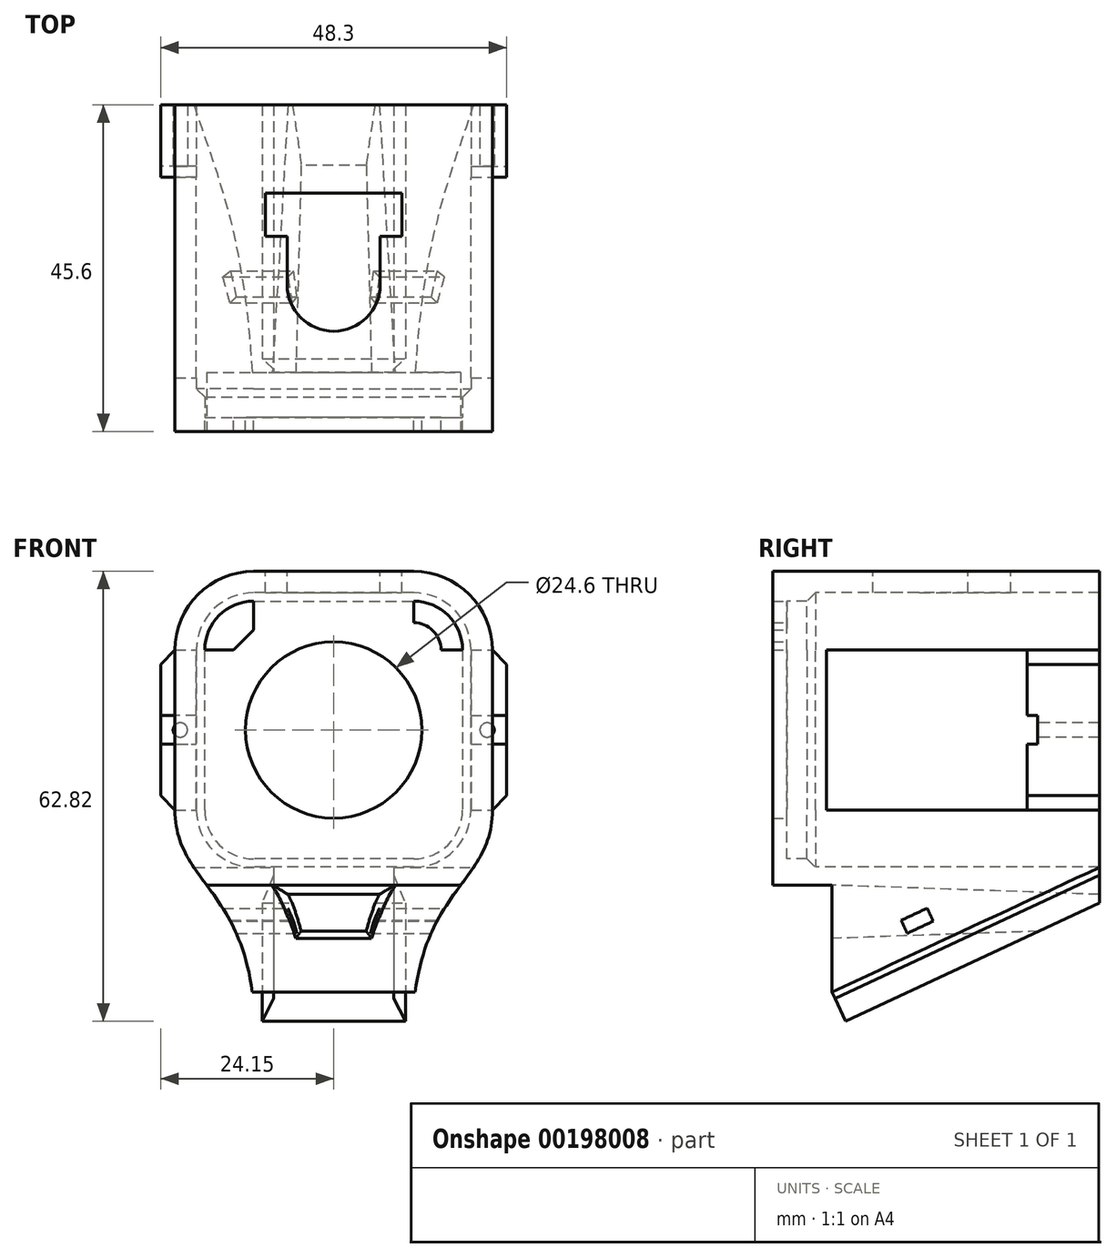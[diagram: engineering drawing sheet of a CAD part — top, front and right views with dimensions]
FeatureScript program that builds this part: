
annotation { "Feature Type Name" : "Feature", "Feature Type Description" : "" }
export const myFeature = defineFeature(function(context is Context, id is Id, definition is map)
    precondition{}
    {
        {
            var Q0;
            Q0=qCreatedBy(makeId("Front.planeOp"),FACE);
            var sketch = newSketch(context, id + "F0", { "sketchPlane" : qUnion([Q0])});
            skLineSegment(sketch, "E0.bottom", {"start": v(11.15, 19.15) * mm, "end": v(-11.15, 19.15) * mm});
            skLineSegment(sketch, "E0.top", {"start": v(11.15, -19.15) * mm, "end": v(-11.15, -19.15) * mm});
            skLineSegment(sketch, "E0.left", {"start": v(19.15, 11.15) * mm, "end": v(19.15, -11.15) * mm});
            skLineSegment(sketch, "E0.right", {"start": v(-19.15, 11.15) * mm, "end": v(-19.15, -11.15) * mm});
            skPoint(sketch, "E0.middle", {"position": v(0, 0) * mm});
            skPoint(sketch, "E1.visualSharp", {"position": v(-19.15, 19.15) * mm});
            skArc(sketch, "E1.filletArc", {"start": v(-11.15, 19.15) * mm, "mid": v(-16.8, 16.8) * mm, "end": v(-19.15, 11.15) * mm});
            skPoint(sketch, "E2.visualSharp", {"position": v(19.15, 19.15) * mm});
            skArc(sketch, "E2.filletArc", {"start": v(19.15, 11.15) * mm, "mid": v(16.8, 16.8) * mm, "end": v(11.15, 19.15) * mm});
            skPoint(sketch, "E3.visualSharp", {"position": v(19.15, -19.15) * mm});
            skArc(sketch, "E3.filletArc", {"start": v(11.15, -19.15) * mm, "mid": v(16.8, -16.8) * mm, "end": v(19.15, -11.15) * mm});
            skPoint(sketch, "E4.visualSharp", {"position": v(-19.15, -19.15) * mm});
            skArc(sketch, "E4.filletArc", {"start": v(-19.15, -11.15) * mm, "mid": v(-16.8, -16.8) * mm, "end": v(-11.15, -19.15) * mm});
            skLineSegment(sketch, "E5.0", {"start": v(11.15, 22.15) * mm, "end": v(-11.15, 22.15) * mm});
            skArc(sketch, "E5.1", {"start": v(22.15, 11.15) * mm, "mid": v(18.93, 18.93) * mm, "end": v(11.15, 22.15) * mm});
            skArc(sketch, "E5.2", {"start": v(-11.15, 22.15) * mm, "mid": v(-18.93, 18.93) * mm, "end": v(-22.15, 11.15) * mm});
            skLineSegment(sketch, "E5.3", {"start": v(22.15, 11.15) * mm, "end": v(22.15, -11.15) * mm});
            skLineSegment(sketch, "E5.4", {"start": v(-22.15, 11.15) * mm, "end": v(-22.15, -11.15) * mm});
            skArc(sketch, "E5.5", {"start": v(-22.15, -11.15) * mm, "mid": v(-18.93, -18.93) * mm, "end": v(-11.15, -22.15) * mm});
            skLineSegment(sketch, "E5.6", {"start": v(11.15, -22.15) * mm, "end": v(-11.15, -22.15) * mm});
            skArc(sketch, "E5.7", {"start": v(11.15, -22.15) * mm, "mid": v(18.93, -18.93) * mm, "end": v(22.15, -11.15) * mm});
            skLineSegment(sketch, "E6.0", {"start": v(11.15, 17.98) * mm, "end": v(-11.15, 17.98) * mm});
            skArc(sketch, "E6.1", {"start": v(17.98, 11.15) * mm, "mid": v(15.98, 15.98) * mm, "end": v(11.15, 17.98) * mm});
            skArc(sketch, "E6.2", {"start": v(-11.15, 17.98) * mm, "mid": v(-15.98, 15.98) * mm, "end": v(-17.98, 11.15) * mm});
            skLineSegment(sketch, "E6.3", {"start": v(17.98, 11.15) * mm, "end": v(17.98, -11.15) * mm});
            skLineSegment(sketch, "E6.4", {"start": v(-17.98, 11.15) * mm, "end": v(-17.98, -11.15) * mm});
            skArc(sketch, "E6.5", {"start": v(-17.98, -11.15) * mm, "mid": v(-15.98, -15.98) * mm, "end": v(-11.15, -17.98) * mm});
            skLineSegment(sketch, "E6.6", {"start": v(11.15, -17.98) * mm, "end": v(-11.15, -17.98) * mm});
            skArc(sketch, "E6.7", {"start": v(11.15, -17.98) * mm, "mid": v(15.98, -15.98) * mm, "end": v(17.98, -11.15) * mm});
            skFitSpline(sketch, "E7", {"points": [v(-22.15, -11.15) * mm, v(-11, -42.15) * mm], "startDerivative": vector(0, -32.02) * mm, "endDerivative": vector(0.45, -60) * mm});
            skLineSegment(sketch, "E8", {"start": v(-22.15, -11.15) * mm, "end": v(-22.15, -23.53) * mm, "construction": true});
            skPoint(sketch, "E9", {"position": v(-22.15, -17.34) * mm});
            skLineSegment(sketch, "E10", {"start": v(-11, -42.15) * mm, "end": v(0, -42.15) * mm});
            skLineSegment(sketch, "E11", {"start": v(0, -42.15) * mm, "end": v(0, -22.15) * mm, "construction": true});
            skLineSegment(sketch, "E12.MirrorCS", {"start": v(11, -42.15) * mm, "end": v(0, -42.15) * mm});
            skFitSpline(sketch, "E13.MirrorCS", {"points": [v(22.15, -11.15) * mm, v(11, -42.15) * mm], "startDerivative": vector(0, -32.02) * mm, "endDerivative": vector(-0.45, -60) * mm});
            skSolve(sketch);
        }
        {
            var Q0;
            Q0=makeQuery(id+"F0.imprint","IMPRINT",FACE,{"disambiguationData":[TD([[makeQuery(id+"F0.imprint","IMPRINT",EDGE,{"derivedFrom":sQuery(id+"F0.wireOp",EDGE,"E0.bottom")}),-1.0]])]});
            var Q1;
            Q1=makeQuery(id+"F0.imprint","IMPRINT",FACE,{"disambiguationData":[TD([[makeQuery(id+"F0.imprint","IMPRINT",EDGE,{"derivedFrom":sQuery(id+"F0.wireOp",EDGE,"E5.5")}),-1.0]])]});
            extrude(context, id + "F1", {"entities" : qUnion([Q0, Q1]), "oppositeDirection" : true, "depth" : 43.6 * mm});
        }
        {
            var Q0;
            Q0=makeQuery(id+"F0.imprint","IMPRINT",FACE,{"disambiguationData":[TD([[makeQuery(id+"F0.imprint","IMPRINT",EDGE,{"derivedFrom":sQuery(id+"F0.wireOp",EDGE,"E0.bottom")}),1.0]])]});
            var Q1;
            Q1=makeQuery(id+"F0.imprint","IMPRINT",FACE,{"disambiguationData":[TD([[makeQuery(id+"F0.imprint","IMPRINT",EDGE,{"derivedFrom":sQuery(id+"F0.wireOp",EDGE,"E0.bottom")}),-1.0]])]});
            extrude(context, id + "F2", {"entities" : qUnion([Q0, Q1]), "operationType" : NewBodyOperationType.ADD, "oppositeDirection" : true, "depth" : 4 * mm});
        }
        {
            var Q0;
            Q0=makeQuery(id+"F2.opExtrude","CAP_EDGE",EDGE,{"disambiguationData":[OSD([sQuery(id+"F0.wireOp",EDGE,"E6.2")])],"isStart":false});
            var Q1;
            Q1=makeQuery(id+"F2.opExtrude","CAP_EDGE",EDGE,{"disambiguationData":[OSD([sQuery(id+"F0.wireOp",EDGE,"E6.4")])],"isStart":false});
            var Q2;
            Q2=makeQuery(id+"F2.opExtrude","CAP_EDGE",EDGE,{"disambiguationData":[OSD([sQuery(id+"F0.wireOp",EDGE,"E6.5")])],"isStart":false});
            var Q3;
            Q3=makeQuery(id+"F2.opExtrude","CAP_EDGE",EDGE,{"disambiguationData":[OSD([sQuery(id+"F0.wireOp",EDGE,"E6.6")])],"isStart":false});
            var Q4;
            Q4=makeQuery(id+"F2.opExtrude","CAP_EDGE",EDGE,{"disambiguationData":[OSD([sQuery(id+"F0.wireOp",EDGE,"E6.7")])],"isStart":false});
            var Q5;
            Q5=makeQuery(id+"F2.opExtrude","CAP_EDGE",EDGE,{"disambiguationData":[OSD([sQuery(id+"F0.wireOp",EDGE,"E6.3")])],"isStart":false});
            var Q6;
            Q6=makeQuery(id+"F2.opExtrude","CAP_EDGE",EDGE,{"disambiguationData":[OSD([sQuery(id+"F0.wireOp",EDGE,"E6.1")])],"isStart":false});
            var Q7;
            Q7=makeQuery(id+"F2.opExtrude","CAP_EDGE",EDGE,{"disambiguationData":[OSD([sQuery(id+"F0.wireOp",EDGE,"E6.0")])],"isStart":false});
            chamfer(context, id + "F3", {"entities" : qUnion([Q0, Q1, Q2, Q3, Q4, Q5, Q6, Q7]), "width" : 1.2 * mm, "tangentPropagation" : true});
        }
        {
            var Q0;
            Q0=makeQuery(id+"F1.opExtrude","SWEPT_FACE",FACE,{"disambiguationData":[OSD([sQuery(id+"F0.wireOp",EDGE,"E5.0")])]});
            var sketch = newSketch(context, id + "F4", { "sketchPlane" : qUnion([Q0])});
            skCircle(sketch, "E14", {"center": v(0, 18.5) * mm, "radius": 6.5 * mm});
            skLineSegment(sketch, "E15.bottom", {"start": v(-9.5, 25.25) * mm, "end": v(9.5, 25.25) * mm});
            skLineSegment(sketch, "E15.top", {"start": v(-9.5, 31.25) * mm, "end": v(9.5, 31.25) * mm});
            skLineSegment(sketch, "E15.left", {"start": v(-9.5, 25.25) * mm, "end": v(-9.5, 31.25) * mm});
            skLineSegment(sketch, "E15.right", {"start": v(9.5, 25.25) * mm, "end": v(9.5, 31.25) * mm});
            skPoint(sketch, "E15.middle", {"position": v(0, 28.25) * mm});
            skLineSegment(sketch, "E16", {"start": v(-6.5, 18.5) * mm, "end": v(-6.5, 25.25) * mm});
            skLineSegment(sketch, "E17", {"start": v(6.5, 18.5) * mm, "end": v(6.5, 25.25) * mm});
            skSolve(sketch);
        }
        {
            var Q0;
            Q0=makeQuery(id+"F4.imprint","IMPRINT",FACE,{"disambiguationData":[TD([[makeQuery(id+"F4.imprint","IMPRINT",EDGE,{"derivedFrom":sQuery(id+"F4.wireOp",EDGE,"E15.bottom")}),1.0]])]});
            var Q1;
            Q1=makeQuery(id+"F4.imprint","IMPRINT",FACE,{"disambiguationData":[TD([[makeQuery(id+"F4.imprint","IMPRINT",EDGE,{"derivedFrom":sQuery(id+"F4.wireOp",EDGE,"E14")}),1.0]])]});
            var Q2;
            {var subQ0=sQuery(id+"F4.wireOp",EDGE,"E16");Q2=makeQuery(id+"F4.imprint","IMPRINT",FACE,{"disambiguationData":[TD([[makeQuery(id+"F4.imprint","IMPRINT",EDGE,{"derivedFrom":subQ0}),-1.0]])]});}
            extrude(context, id + "F5", {"entities" : qUnion([Q0, Q1, Q2]), "operationType" : NewBodyOperationType.REMOVE, "oppositeDirection" : true, "depth" : 5 * mm});
        }
        {
            var Q0;
            Q0=makeQuery(id+"F1.opExtrude","SWEPT_FACE",FACE,{"disambiguationData":[OSD([sQuery(id+"F0.wireOp",EDGE,"E5.3")])]});
            var sketch = newSketch(context, id + "F6", { "sketchPlane" : qUnion([Q0])});
            skLineSegment(sketch, "E18", {"start": v(5.5, 11.15) * mm, "end": v(5.5, -11.15) * mm});
            skLineSegment(sketch, "E19", {"start": v(33.5, 11.15) * mm, "end": v(33.5, -11.15) * mm});
            skLineSegment(sketch, "E20.bottom", {"start": v(1.66, -73.43) * mm, "end": v(54.98, -48.56) * mm});
            skLineSegment(sketch, "E20.top", {"start": v(-9.73, -49.02) * mm, "end": v(43.6, -24.15) * mm});
            skLineSegment(sketch, "E20.left", {"start": v(1.66, -73.43) * mm, "end": v(-9.73, -49.02) * mm});
            skLineSegment(sketch, "E20.right", {"start": v(54.98, -48.56) * mm, "end": v(43.6, -24.15) * mm});
            skLineSegment(sketch, "E21", {"start": v(-9.73, -21.65) * mm, "end": v(6.28, -21.65) * mm});
            skLineSegment(sketch, "E22", {"start": v(6.28, -21.65) * mm, "end": v(6.28, -41.55) * mm});
            skLineSegment(sketch, "E23", {"start": v(-9.73, -49.02) * mm, "end": v(-9.73, -21.65) * mm});
            skLineSegment(sketch, "E24", {"start": v(8.18, -40.67) * mm, "end": v(6.28, -36.59) * mm});
            skLineSegment(sketch, "E25", {"start": v(0, -21.65) * mm, "end": v(0, -44.48) * mm});
            skLineSegment(sketch, "E26", {"start": v(15.95, -26.56) * mm, "end": v(16.8, -28.38) * mm});
            skLineSegment(sketch, "E27", {"start": v(16.8, -28.38) * mm, "end": v(20.42, -26.69) * mm});
            skLineSegment(sketch, "E28", {"start": v(20.42, -26.69) * mm, "end": v(19.57, -24.87) * mm});
            skLineSegment(sketch, "E29", {"start": v(19.57, -24.87) * mm, "end": v(15.95, -26.56) * mm});
            skSolve(sketch);
        }
        {
            var Q0;
            {var subQ0=sQuery(id+"F6.wireOp",EDGE,"E18");Q0=makeQuery(id+"F6.imprint","IMPRINT",FACE,{"disambiguationData":[TD([[makeQuery(id+"F6.imprint","IMPRINT",EDGE,{"derivedFrom":subQ0}),1.0]])]});}
            extrude(context, id + "F7", {"entities" : qUnion([Q0]), "operationType" : NewBodyOperationType.REMOVE, "oppositeDirection" : true, "depth" : 45 * mm});
        }
        {
            var Q0;
            {var subQ2=sQuery(id+"F6.wireOp",EDGE,"1458fb0b-f914-4daf-8312-8bd524e81ef2");Q0=makeQuery(id+"F6.imprint","IMPRINT",FACE,{"disambiguationData":[TD([[makeQuery(id+"F6.imprint","IMPRINT",EDGE,{"derivedFrom":subQ2}),-1.0]])]});}
            var Q1;
            {var subQ3=sQuery(id+"F6.wireOp",EDGE,"E24");Q1=makeQuery(id+"F6.imprint","IMPRINT",FACE,{"disambiguationData":[TD([[makeQuery(id+"F6.imprint","IMPRINT",EDGE,{"derivedFrom":subQ3}),1.0]])]});}
            var Q2;
            Q2=makeQuery(id+"F6.imprint","IMPRINT",FACE,{"disambiguationData":[TD([[makeQuery(id+"F6.imprint","IMPRINT",EDGE,{"derivedFrom":sQuery(id+"F6.wireOp",EDGE,"E20.bottom")}),1.0]])]});
            var Q3;
            {var subQ6=sQuery(id+"F6.wireOp",EDGE,"E25");Q3=makeQuery(id+"F6.imprint","IMPRINT",FACE,{"disambiguationData":[TD([[makeQuery(id+"F6.imprint","IMPRINT",EDGE,{"derivedFrom":subQ6}),1.0]])]});}
            extrude(context, id + "F8", {"entities" : qUnion([Q0, Q1, Q2, Q3]), "operationType" : NewBodyOperationType.REMOVE, "endBound" : BoundingType.THROUGH_ALL, "oppositeDirection" : true, "depth" : 80 * mm});
        }
        {
            var Q0;
            Q0=makeQuery(id+"F8.boolean.opBoolean","COPY",FACE,{"derivedFrom":makeQuery(id+"F8.opExtrude","SWEPT_FACE",FACE,{"disambiguationData":[OSD([sQuery(id+"F6.wireOp",EDGE,"E24")])]})});
            var sketch = newSketch(context, id + "F9", { "sketchPlane" : qUnion([Q0])});
            skLineSegment(sketch, "E30", {"start": v(-8.37, -35.81) * mm, "end": v(-8.37, -36.81) * mm});
            skLineSegment(sketch, "E31", {"start": v(-8.37, -36.81) * mm, "end": v(-10, -40.31) * mm});
            skLineSegment(sketch, "E32", {"start": v(0, -40.31) * mm, "end": v(0, -35.81) * mm, "construction": true});
            skLineSegment(sketch, "E33.MirrorCS", {"start": v(8.37, -35.81) * mm, "end": v(8.37, -36.81) * mm});
            skLineSegment(sketch, "E34.MirrorCS", {"start": v(8.37, -36.81) * mm, "end": v(10, -40.31) * mm});
            skLineSegment(sketch, "E35", {"start": v(-10, -40.31) * mm, "end": v(-27.53, -40.31) * mm});
            skLineSegment(sketch, "E36", {"start": v(-27.53, -40.31) * mm, "end": v(-27.53, -35.81) * mm});
            skLineSegment(sketch, "E37", {"start": v(-27.53, -35.81) * mm, "end": v(-8.37, -35.81) * mm});
            skLineSegment(sketch, "E38.MirrorCS", {"start": v(27.53, -35.81) * mm, "end": v(8.37, -35.81) * mm});
            skLineSegment(sketch, "E39.MirrorCS", {"start": v(10, -40.31) * mm, "end": v(27.53, -40.31) * mm});
            skLineSegment(sketch, "E40.MirrorCS", {"start": v(27.53, -40.31) * mm, "end": v(27.53, -35.81) * mm});
            skSolve(sketch);
        }
        {
            var Q0;
            {var subQ4=sQuery(id+"F9.wireOp",EDGE,"E30");Q0=makeQuery(id+"F9.imprint","IMPRINT",FACE,{"disambiguationData":[TD([[makeQuery(id+"F9.imprint","IMPRINT",EDGE,{"derivedFrom":subQ4}),-1.0]])]});}
            var Q1;
            {var subQ4=sQuery(id+"F9.wireOp",EDGE,"E33.MirrorCS");Q1=makeQuery(id+"F9.imprint","IMPRINT",FACE,{"disambiguationData":[TD([[makeQuery(id+"F9.imprint","IMPRINT",EDGE,{"derivedFrom":subQ4}),1.0]])]});}
            var Q2;
            {var subQ2=sQuery(id+"F9.wireOp",EDGE,"E36");Q2=makeQuery(id+"F9.imprint","IMPRINT",FACE,{"disambiguationData":[TD([[makeQuery(id+"F9.imprint","IMPRINT",EDGE,{"derivedFrom":subQ2}),-1.0]])]});}
            var Q3;
            {var subQ2=sQuery(id+"F9.wireOp",EDGE,"E40.MirrorCS");Q3=makeQuery(id+"F9.imprint","IMPRINT",FACE,{"disambiguationData":[TD([[makeQuery(id+"F9.imprint","IMPRINT",EDGE,{"derivedFrom":subQ2}),1.0]])]});}
            extrude(context, id + "F10", {"entities" : qUnion([Q0, Q1, Q2, Q3]), "operationType" : NewBodyOperationType.REMOVE, "endBound" : BoundingType.THROUGH_ALL, "oppositeDirection" : true, "depth" : 25 * mm});
        }
        {
            var Q0;
            {var subQ0=sQuery(id+"F0.wireOp",EDGE,"E5.4");var subQ1=sQuery(id+"F0.wireOp",EDGE,"E5.3");var subQ2=sQuery(id+"F0.wireOp",EDGE,"E5.2");var subQ3=sQuery(id+"F0.wireOp",EDGE,"E5.1");var subQ4=sQuery(id+"F0.wireOp",EDGE,"E5.0");Q0=makeQuery(id+"F2.boolean.opBoolean","MERGE",FACE,{"derivedFrom":[makeQuery(id+"F1.opExtrude","CAP_FACE",FACE,{"disambiguationData":[OSD([sQuery(id+"F0.wireOp",EDGE,"E0.bottom"),sQuery(id+"F0.wireOp",EDGE,"E0.top"),sQuery(id+"F0.wireOp",EDGE,"E0.left"),sQuery(id+"F0.wireOp",EDGE,"E0.right"),sQuery(id+"F0.wireOp",EDGE,"E1.filletArc"),sQuery(id+"F0.wireOp",EDGE,"E2.filletArc"),sQuery(id+"F0.wireOp",EDGE,"E3.filletArc"),sQuery(id+"F0.wireOp",EDGE,"E4.filletArc"),subQ4,subQ3,subQ2,subQ1,subQ0,sQuery(id+"F0.wireOp",EDGE,"E7"),sQuery(id+"F0.wireOp",EDGE,"E10"),sQuery(id+"F0.wireOp",EDGE,"E12.MirrorCS"),sQuery(id+"F0.wireOp",EDGE,"E13.MirrorCS")])],"isStart":true}),makeQuery(id+"F2.opExtrude","CAP_FACE",FACE,{"disambiguationData":[OSD([subQ4,subQ3,subQ2,subQ1,subQ0,sQuery(id+"F0.wireOp",EDGE,"E5.5"),sQuery(id+"F0.wireOp",EDGE,"E5.6"),sQuery(id+"F0.wireOp",EDGE,"E5.7"),sQuery(id+"F0.wireOp",EDGE,"E6.0"),sQuery(id+"F0.wireOp",EDGE,"E6.1"),sQuery(id+"F0.wireOp",EDGE,"E6.2"),sQuery(id+"F0.wireOp",EDGE,"E6.3"),sQuery(id+"F0.wireOp",EDGE,"E6.4"),sQuery(id+"F0.wireOp",EDGE,"E6.5"),sQuery(id+"F0.wireOp",EDGE,"E6.6"),sQuery(id+"F0.wireOp",EDGE,"E6.7")])],"isStart":true})]});}
            var sketch = newSketch(context, id + "F11", { "sketchPlane" : qUnion([Q0])});
            skCircle(sketch, "E41", {"center": v(0, 0) * mm, "radius": 12.3 * mm});
            skArc(sketch, "E42.0", {"start": v(14.98, 11.15) * mm, "mid": v(13.86, 13.86) * mm, "end": v(11.15, 14.98) * mm});
            skLineSegment(sketch, "E43", {"start": v(11.15, 14.98) * mm, "end": v(11.15, 17.98) * mm});
            skLineSegment(sketch, "E44", {"start": v(14.98, 11.15) * mm, "end": v(17.98, 11.15) * mm});
            skLineSegment(sketch, "E45", {"start": v(0, 17.98) * mm, "end": v(0, -17.98) * mm, "construction": true});
            skLineSegment(sketch, "E46", {"start": v(-17.98, 11.15) * mm, "end": v(-13.99, 11.15) * mm});
            skLineSegment(sketch, "E47", {"start": v(-11.15, 17.98) * mm, "end": v(-11.15, 13.99) * mm});
            skLineSegment(sketch, "E48", {"start": v(-13.99, 11.15) * mm, "end": v(-11.15, 13.99) * mm});
            skSolve(sketch);
        }
        {
            var Q0;
            Q0=makeQuery(id+"F11.imprint","IMPRINT",FACE,{"disambiguationData":[TD([[makeQuery(id+"F11.imprint","IMPRINT",EDGE,{"derivedFrom":sQuery(id+"F11.wireOp",EDGE,"E41")}),-1.0]])]});
            var Q1;
            {var subQ5=sQuery(id+"F0.wireOp",EDGE,"E5.0");Q1=makeQuery(id+"F11.imprint","IMPRINT",FACE,{"disambiguationData":[TD([[makeQuery(id+"F11.imprint","IMPRINT",EDGE,{"derivedFrom":makeQuery(id+"F1.opExtrude","CAP_EDGE",EDGE,{"disambiguationData":[OSD([subQ5])],"isStart":true})}),1.0]])]});}
            extrude(context, id + "F12", {"entities" : qUnion([Q0, Q1]), "operationType" : NewBodyOperationType.ADD, "depth" : 2 * mm});
        }
        {
            var Q0;
            {var subQ1=sQuery(id+"F0.wireOp",EDGE,"E5.3");Q0=makeQuery(id+"F7.boolean.opBoolean","SPLIT",FACE,{"disambiguationData":[TD([makeQuery(id+"F7.opExtrude","SWEPT_FACE",FACE,{"disambiguationData":[OSD([sQuery(id+"F6.wireOp",EDGE,"E19")])]})])],"derivedFrom":makeQuery(id+"F1.opExtrude","SWEPT_FACE",FACE,{"disambiguationData":[OSD([subQ1])]})});}
            extrude(context, id + "F13", {"entities" : qUnion([Q0]), "operationType" : NewBodyOperationType.ADD, "depth" : 2 * mm});
        }
        {
            var Q0;
            {var subQ0=sQuery(id+"F6.wireOp",EDGE,"E19");Q0=makeQuery(id+"F13.boolean.opBoolean","MERGE",FACE,{"derivedFrom":[makeQuery(id+"F7.boolean.opBoolean","COPY",FACE,{"disambiguationData":[TD([makeQuery(id+"F1.opExtrude","SWEPT_FACE",FACE,{"disambiguationData":[OSD([sQuery(id+"F0.wireOp",EDGE,"E0.left")])]})])],"derivedFrom":makeQuery(id+"F7.opExtrude","SWEPT_FACE",FACE,{"disambiguationData":[OSD([subQ0])]})}),makeQuery(id+"F13.opExtrude","SWEPT_FACE",FACE,{"disambiguationData":[OSD([subQ0])]})]});}
            var sketch = newSketch(context, id + "F14", { "sketchPlane" : qUnion([Q0])});
            skPoint(sketch, "E49", {"position": v(21.4, 0) * mm});
            skLineSegment(sketch, "E50", {"start": v(19.15, 2) * mm, "end": v(24.15, 2) * mm});
            skLineSegment(sketch, "E51", {"start": v(19.15, -2) * mm, "end": v(24.15, -2) * mm});
            skSolve(sketch);
        }
        {
            var Q0;
            Q0=makeQuery(id+"F13.opExtrude","CAP_EDGE",EDGE,{"disambiguationData":[OSD([sQuery(id+"F0.wireOp",EDGE,"E5.1"),sQuery(id+"F0.wireOp",EDGE,"E5.3")])],"isStart":false});
            var Q1;
            Q1=makeQuery(id+"F13.opExtrude","CAP_EDGE",EDGE,{"disambiguationData":[OSD([sQuery(id+"F0.wireOp",EDGE,"E5.3"),sQuery(id+"F0.wireOp",EDGE,"E5.7"),sQuery(id+"F0.wireOp",EDGE,"E13.MirrorCS")])],"isStart":false});
            chamfer(context, id + "F15", {"entities" : qUnion([Q0, Q1]), "width" : 2 * mm, "tangentPropagation" : true});
        }
        {
            var Q0;
            Q0=sQuery(id+"F14.wireOp",VERTEX,"E49");
            var Q1;
            Q1=makeQuery(id+"F1.opExtrude","SWEPT_BODY",BODY,{"disambiguationData":[OSD([sQuery(id+"F0.wireOp",EDGE,"E0.bottom"),sQuery(id+"F0.wireOp",EDGE,"E0.top"),sQuery(id+"F0.wireOp",EDGE,"E0.left"),sQuery(id+"F0.wireOp",EDGE,"E0.right"),sQuery(id+"F0.wireOp",EDGE,"E1.filletArc"),sQuery(id+"F0.wireOp",EDGE,"E2.filletArc"),sQuery(id+"F0.wireOp",EDGE,"E3.filletArc"),sQuery(id+"F0.wireOp",EDGE,"E4.filletArc"),sQuery(id+"F0.wireOp",EDGE,"E5.0"),sQuery(id+"F0.wireOp",EDGE,"E5.1"),sQuery(id+"F0.wireOp",EDGE,"E5.2"),sQuery(id+"F0.wireOp",EDGE,"E5.3"),sQuery(id+"F0.wireOp",EDGE,"E5.4"),sQuery(id+"F0.wireOp",EDGE,"E7"),sQuery(id+"F0.wireOp",EDGE,"E10"),sQuery(id+"F0.wireOp",EDGE,"E12.MirrorCS"),sQuery(id+"F0.wireOp",EDGE,"E13.MirrorCS")])]});
            hole(context, id + "F16", {"style" : HoleStyle.SIMPLE, "endStyle" : HoleEndStyle.THROUGH, "holeDiameter" : 2 * mm, "locations" : qUnion([Q0]), "scope" : qUnion([Q1]), "isTappedThrough" : true});
        }
        {
            var Q0;
            {var subQ0=sQuery(id+"F14.wireOp",EDGE,"E50");Q0=makeQuery(id+"F14.imprint","IMPRINT",FACE,{"disambiguationData":[TD([[makeQuery(id+"F14.imprint","IMPRINT",EDGE,{"derivedFrom":subQ0}),-1.0]])]});}
            extrude(context, id + "F17", {"entities" : qUnion([Q0]), "operationType" : NewBodyOperationType.REMOVE, "oppositeDirection" : true, "depth" : 1.5 * mm});
        }
        {
            var Q0;
            {var subQ2=sQuery(id+"F0.wireOp",EDGE,"E5.4");Q0=makeQuery(id+"F7.boolean.opBoolean","SPLIT",FACE,{"disambiguationData":[TD([makeQuery(id+"F7.opExtrude","SWEPT_FACE",FACE,{"disambiguationData":[OSD([sQuery(id+"F6.wireOp",EDGE,"E19")])]})])],"derivedFrom":makeQuery(id+"F1.opExtrude","SWEPT_FACE",FACE,{"disambiguationData":[OSD([subQ2])]})});}
            extrude(context, id + "F18", {"entities" : qUnion([Q0]), "operationType" : NewBodyOperationType.ADD, "depth" : 2 * mm});
        }
        {
            var Q0;
            {var subQ0=sQuery(id+"F6.wireOp",EDGE,"E19");var subQ1=sQuery(id+"F0.wireOp",EDGE,"E5.4");Q0=makeQuery(id+"F18.boolean.opBoolean","MERGE",FACE,{"derivedFrom":[makeQuery(id+"F7.boolean.opBoolean","COPY",FACE,{"disambiguationData":[TD([makeQuery(id+"F1.opExtrude","SWEPT_FACE",FACE,{"disambiguationData":[OSD([sQuery(id+"F0.wireOp",EDGE,"E0.right")])]})])],"derivedFrom":makeQuery(id+"F7.opExtrude","SWEPT_FACE",FACE,{"disambiguationData":[OSD([subQ0])]})}),makeQuery(id+"F18.opExtrude","SWEPT_FACE",FACE,{"disambiguationData":[OSD([subQ1,subQ0])]})]});}
            var sketch = newSketch(context, id + "F19", { "sketchPlane" : qUnion([Q0])});
            skPoint(sketch, "E52.0.midPoint", {"position": v(-19.15, 0) * mm});
            skPoint(sketch, "E53", {"position": v(-21.4, 0) * mm});
            skLineSegment(sketch, "E54", {"start": v(-19.15, 2) * mm, "end": v(-24.15, 2) * mm});
            skLineSegment(sketch, "E55", {"start": v(-24.15, -2) * mm, "end": v(-19.15, -2) * mm});
            skSolve(sketch);
        }
        {
            var Q0;
            Q0=makeQuery(id+"F18.opExtrude","CAP_EDGE",EDGE,{"disambiguationData":[OSD([sQuery(id+"F0.wireOp",EDGE,"E5.2"),sQuery(id+"F0.wireOp",EDGE,"E5.4")])],"isStart":false});
            var Q1;
            Q1=makeQuery(id+"F18.opExtrude","CAP_EDGE",EDGE,{"disambiguationData":[OSD([sQuery(id+"F0.wireOp",EDGE,"E5.4"),sQuery(id+"F0.wireOp",EDGE,"E5.5"),sQuery(id+"F0.wireOp",EDGE,"E7")])],"isStart":false});
            chamfer(context, id + "F20", {"entities" : qUnion([Q0, Q1]), "width" : 2 * mm, "tangentPropagation" : true});
        }
        {
            var Q0;
            Q0=sQuery(id+"F19.wireOp",VERTEX,"E53");
            var Q1;
            Q1=makeQuery(id+"F1.opExtrude","SWEPT_BODY",BODY,{"disambiguationData":[OSD([sQuery(id+"F0.wireOp",EDGE,"E0.bottom"),sQuery(id+"F0.wireOp",EDGE,"E0.top"),sQuery(id+"F0.wireOp",EDGE,"E0.left"),sQuery(id+"F0.wireOp",EDGE,"E0.right"),sQuery(id+"F0.wireOp",EDGE,"E1.filletArc"),sQuery(id+"F0.wireOp",EDGE,"E2.filletArc"),sQuery(id+"F0.wireOp",EDGE,"E3.filletArc"),sQuery(id+"F0.wireOp",EDGE,"E4.filletArc"),sQuery(id+"F0.wireOp",EDGE,"E5.0"),sQuery(id+"F0.wireOp",EDGE,"E5.1"),sQuery(id+"F0.wireOp",EDGE,"E5.2"),sQuery(id+"F0.wireOp",EDGE,"E5.3"),sQuery(id+"F0.wireOp",EDGE,"E5.4"),sQuery(id+"F0.wireOp",EDGE,"E7"),sQuery(id+"F0.wireOp",EDGE,"E10"),sQuery(id+"F0.wireOp",EDGE,"E12.MirrorCS"),sQuery(id+"F0.wireOp",EDGE,"E13.MirrorCS")])]});
            hole(context, id + "F21", {"style" : HoleStyle.SIMPLE, "endStyle" : HoleEndStyle.THROUGH, "holeDiameter" : 2 * mm, "locations" : qUnion([Q0]), "scope" : qUnion([Q1]), "isTappedThrough" : true});
        }
        {
            var Q0;
            {var subQ0=sQuery(id+"F19.wireOp",EDGE,"E54");Q0=makeQuery(id+"F19.imprint","IMPRINT",FACE,{"disambiguationData":[TD([[makeQuery(id+"F19.imprint","IMPRINT",EDGE,{"derivedFrom":subQ0}),1.0]])]});}
            extrude(context, id + "F22", {"entities" : qUnion([Q0]), "operationType" : NewBodyOperationType.REMOVE, "oppositeDirection" : true, "depth" : 1.5 * mm});
        }
        {
            var Q0;
            Q0=makeQuery(id+"F8.boolean.opBoolean","COPY",FACE,{"derivedFrom":makeQuery(id+"F8.opExtrude","SWEPT_FACE",FACE,{"disambiguationData":[OSD([sQuery(id+"F6.wireOp",EDGE,"E22")])]})});
            var sketch = newSketch(context, id + "F23", { "sketchPlane" : qUnion([Q0])});
            skLineSegment(sketch, "E56.0", {"start": v(-6.4, -29.09) * mm, "end": v(6.4, -29.09) * mm});
            skPoint(sketch, "E57", {"position": v(-9.87, -31.59) * mm});
            skFitSpline(sketch, "E58.0", {"points": [v(-3.5, -42.1) * mm, v(-3.52, -39.25) * mm, v(-3.84, -35.38) * mm, v(-4.78, -30.89) * mm, v(-5.7, -27.84) * mm, v(-6.8, -25.11) * mm, v(-8.42, -21.9) * mm, v(-10.15, -19.3) * mm, v(-11.66, -17.23) * mm, v(-12.63, -15.93) * mm, v(-13.38, -14.86) * mm, v(-13.92, -13.99) * mm, v(-14.26, -13.3) * mm, v(-14.47, -12.7) * mm, v(-14.6, -12.06) * mm, v(-14.65, -11.5) * mm, v(-14.65, -11.15) * mm]});
            skFitSpline(sketch, "E59.0", {"points": [v(3.5, -42.1) * mm, v(3.52, -39.25) * mm, v(3.84, -35.38) * mm, v(4.78, -30.89) * mm, v(5.7, -27.84) * mm, v(6.8, -25.11) * mm, v(8.42, -21.9) * mm, v(10.15, -19.3) * mm, v(11.66, -17.23) * mm, v(12.63, -15.93) * mm, v(13.38, -14.86) * mm, v(13.92, -13.99) * mm, v(14.26, -13.3) * mm, v(14.47, -12.7) * mm, v(14.6, -12.06) * mm, v(14.65, -11.5) * mm, v(14.65, -11.15) * mm]});
            skSolve(sketch);
        }
        {
            var Q0;
            {var subQ0=sQuery(id+"F23.wireOp",EDGE,"E58.0");var subQ1=sQuery(id+"F23.wireOp",EDGE,"E56.0");var subQ2=makeQuery(id+"F23.imprint","INTERSECT",VERTEX,{"derivedFrom":[subQ1,subQ0]});Q0=makeQuery(id+"F23.imprint","IMPRINT",FACE,{"disambiguationData":[TD([[makeQuery(id+"F23.imprint","IMPRINT",EDGE,{"disambiguationData":[TD([[subQ2,-1.0]])],"derivedFrom":subQ1}),1.0]])]});}
            extrude(context, id + "F24", {"entities" : qUnion([Q0]), "operationType" : NewBodyOperationType.REMOVE, "endBound" : BoundingType.THROUGH_ALL, "oppositeDirection" : true, "depth" : 25 * mm, "hasDraft" : true, "draftAngle" : 2 * degree, "draftPullDirection" : true});
        }
        {
            var Q0;
            Q0=makeQuery(id+"F6.imprint","IMPRINT",FACE,{"disambiguationData":[TD([[makeQuery(id+"F6.imprint","IMPRINT",EDGE,{"derivedFrom":sQuery(id+"F6.wireOp",EDGE,"E26")}),1.0]])]});
            extrude(context, id + "F25", {"entities" : qUnion([Q0]), "operationType" : NewBodyOperationType.REMOVE, "endBound" : BoundingType.THROUGH_ALL, "oppositeDirection" : true, "depth" : 25 * mm});
        }
    });
